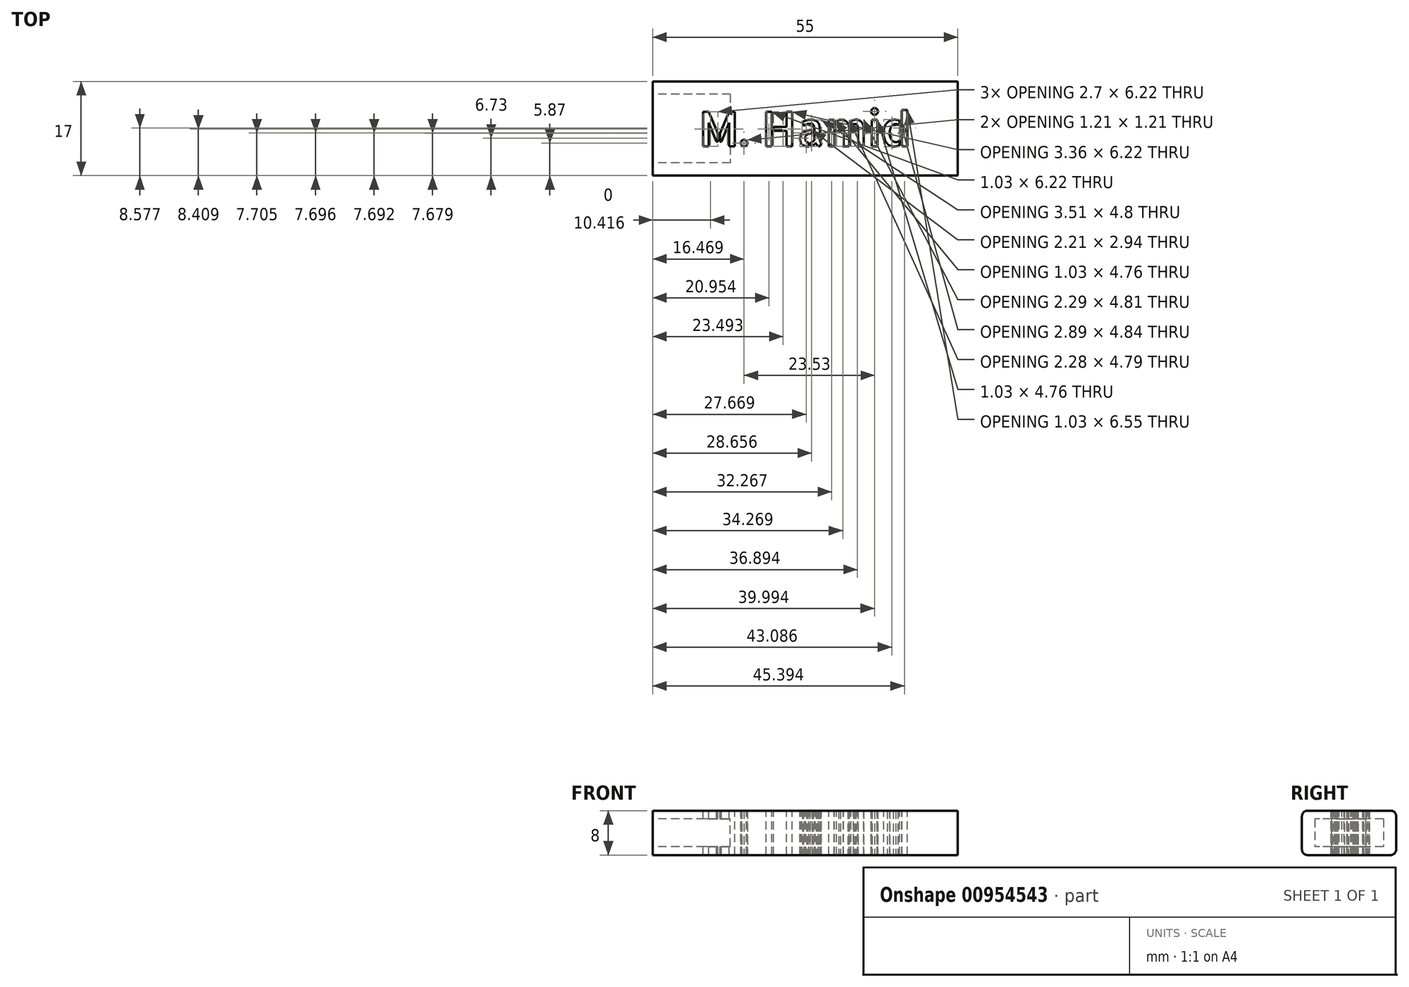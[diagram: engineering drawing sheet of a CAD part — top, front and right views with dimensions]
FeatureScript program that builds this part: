
annotation { "Feature Type Name" : "Feature", "Feature Type Description" : "" }
export const myFeature = defineFeature(function(context is Context, id is Id, definition is map)
    precondition{}
    {
        {
            var Q0;
            Q0=qCreatedBy(makeId("Front.planeOp"),FACE);
            var sketch = newSketch(context, id + "F0", { "sketchPlane" : qUnion([Q0])});
            skLineSegment(sketch, "E0.bottom", {"start": v(-7.5, 4) * mm, "end": v(7.5, 4) * mm});
            skLineSegment(sketch, "E0.top", {"start": v(-7.5, -4) * mm, "end": v(7.5, -4) * mm});
            skLineSegment(sketch, "E0.left", {"start": v(-8.5, 3) * mm, "end": v(-8.5, -3) * mm});
            skLineSegment(sketch, "E0.right", {"start": v(8.5, 3) * mm, "end": v(8.5, -3) * mm});
            skPoint(sketch, "E0.middle", {"position": v(0, 0) * mm});
            skPoint(sketch, "E1.visualSharp", {"position": v(-8.5, 4) * mm});
            skArc(sketch, "E1.filletArc", {"start": v(-7.5, 4) * mm, "mid": v(-8.2, 3.7) * mm, "end": v(-8.5, 3) * mm});
            skPoint(sketch, "E2.visualSharp", {"position": v(8.5, 4) * mm});
            skArc(sketch, "E2.filletArc", {"start": v(8.5, 3) * mm, "mid": v(8.2, 3.7) * mm, "end": v(7.5, 4) * mm});
            skPoint(sketch, "E3.visualSharp", {"position": v(-8.5, -4) * mm});
            skArc(sketch, "E3.filletArc", {"start": v(-8.5, -3) * mm, "mid": v(-8.2, -3.7) * mm, "end": v(-7.5, -4) * mm});
            skPoint(sketch, "E4.visualSharp", {"position": v(8.5, -4) * mm});
            skArc(sketch, "E4.filletArc", {"start": v(7.5, -4) * mm, "mid": v(8.2, -3.7) * mm, "end": v(8.5, -3) * mm});
            skSolve(sketch);
        }
        {
            var Q0;
            Q0 = qSketchRegion(id + "F0", true);
            extrude(context, id + "F1", {"entities" : qUnion([Q0]), "depth" : 55 * mm, "offsetDistance" : 25 * mm});
        }
        {
            var Q0;
            Q0=makeQuery(id+"F1.opExtrude","CAP_FACE",FACE,{"disambiguationData":[OSD([sQuery(id+"F0.wireOp",EDGE,"E0.bottom"),sQuery(id+"F0.wireOp",EDGE,"E0.top"),sQuery(id+"F0.wireOp",EDGE,"E0.left"),sQuery(id+"F0.wireOp",EDGE,"E0.right"),sQuery(id+"F0.wireOp",EDGE,"E1.filletArc"),sQuery(id+"F0.wireOp",EDGE,"E2.filletArc"),sQuery(id+"F0.wireOp",EDGE,"E3.filletArc"),sQuery(id+"F0.wireOp",EDGE,"E4.filletArc")])],"isStart":false});
            var sketch = newSketch(context, id + "F2", { "sketchPlane" : qUnion([Q0])});
            skLineSegment(sketch, "E5.bottom", {"start": v(-6.2, 2.5) * mm, "end": v(6.2, 2.5) * mm});
            skLineSegment(sketch, "E5.top", {"start": v(-6.2, -2.5) * mm, "end": v(6.2, -2.5) * mm});
            skLineSegment(sketch, "E5.left", {"start": v(-6.2, 2.5) * mm, "end": v(-6.2, -2.5) * mm});
            skLineSegment(sketch, "E5.right", {"start": v(6.2, 2.5) * mm, "end": v(6.2, -2.5) * mm});
            skPoint(sketch, "E5.middle", {"position": v(0, 0) * mm});
            skSolve(sketch);
        }
        {
            var Q0;
            Q0 = qSketchRegion(id + "F2", true);
            extrude(context, id + "F3", {"entities" : qUnion([Q0]), "operationType" : NewBodyOperationType.REMOVE, "oppositeDirection" : true, "depth" : 14 * mm, "offsetDistance" : 25 * mm});
        }
        {
            var Q0;
            Q0=makeQuery(id+"F1.opExtrude","SWEPT_BODY",BODY,{"disambiguationData":[OSD([sQuery(id+"F0.wireOp",EDGE,"E0.bottom"),sQuery(id+"F0.wireOp",EDGE,"E0.top"),sQuery(id+"F0.wireOp",EDGE,"E0.left"),sQuery(id+"F0.wireOp",EDGE,"E0.right"),sQuery(id+"F0.wireOp",EDGE,"E1.filletArc"),sQuery(id+"F0.wireOp",EDGE,"E2.filletArc"),sQuery(id+"F0.wireOp",EDGE,"E3.filletArc"),sQuery(id+"F0.wireOp",EDGE,"E4.filletArc")])]});
            var Q1;
            Q1=makeQuery(id+"F1.opExtrude","CAP_EDGE",EDGE,{"disambiguationData":[OSD([sQuery(id+"F0.wireOp",EDGE,"E0.left")])],"isStart":true});
            transform(context, id + "F4", {"entities" : qUnion([Q0]), "transformType" : TransformType.ROTATION, "transformAxis" : qUnion([Q1]), "angle" : 90 * degree, "makeCopy" : false});
        }
        {
            var Q0;
            Q0=makeQuery(id+"F1.opExtrude","SWEPT_FACE",FACE,{"disambiguationData":[OSD([sQuery(id+"F0.wireOp",EDGE,"E0.bottom")])]});
            var sketch = newSketch(context, id + "F5", { "sketchPlane" : qUnion([Q0])});
            skText(sketch, "E6", { "text": "M. Hamid", "fontName": "AllertaStencil-Regular.ttf"});
            const initialGuessF5  = {"E6": [-0.05521, -0.0117, 1, 0, 0.00622]};
            skSetInitialGuess(sketch, initialGuessF5);
            skSolve(sketch);
        }
        {
            var Q0;
            Q0 = qSketchRegion(id + "F5", true);
            extrude(context, id + "F6", {"entities" : qUnion([Q0]), "operationType" : NewBodyOperationType.REMOVE, "oppositeDirection" : true, "depth" : 25 * mm, "offsetDistance" : 25 * mm});
        }
    });
